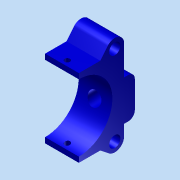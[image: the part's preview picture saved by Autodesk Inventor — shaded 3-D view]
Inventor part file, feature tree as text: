
AUTODESK INVENTOR PART (.ipt)
format: ipt  version: 2012 (Build 160160000, 160)  size: 145,408 bytes
history: native  units: in
note: dims shown in document units (in); Inventor stores cm internally (conversion verified against a paired STEP export)
features: extrude x3, sketch x3
ambient origin geometry x8: Origin, YZ Plane, XZ Plane, XY Plane, X Axis, Y Axis, Z Axis, Center Point
bodies: Solid1 (feature_tree)
feature tree (6):
  extrude  "Extrusion1"  Depth=0.21in
  extrude  "Extrusion2"  Depth=0.35in
  extrude  "Extrusion4"  Depth=1.25in
  sketch  "Sketch2"  dims[d0=0.21in d1=0.21in]
  sketch  "Sketch3"  dims[d2=1.5in d3=0.35in]
  sketch  "Sketch6"  dims[d4=0.35in d7=1.25in d8=0.375in d9=0.55in d10=0.2in d11=0.1in d12=0.1in d13=0.4in d14=0.63in d15=0.0in d16=0.1in d17=0.315in d18=0.1in d19=0.63in d20=0.0in d24=0.125in d25=0.25in d26=1.0in d27=0.0in]
